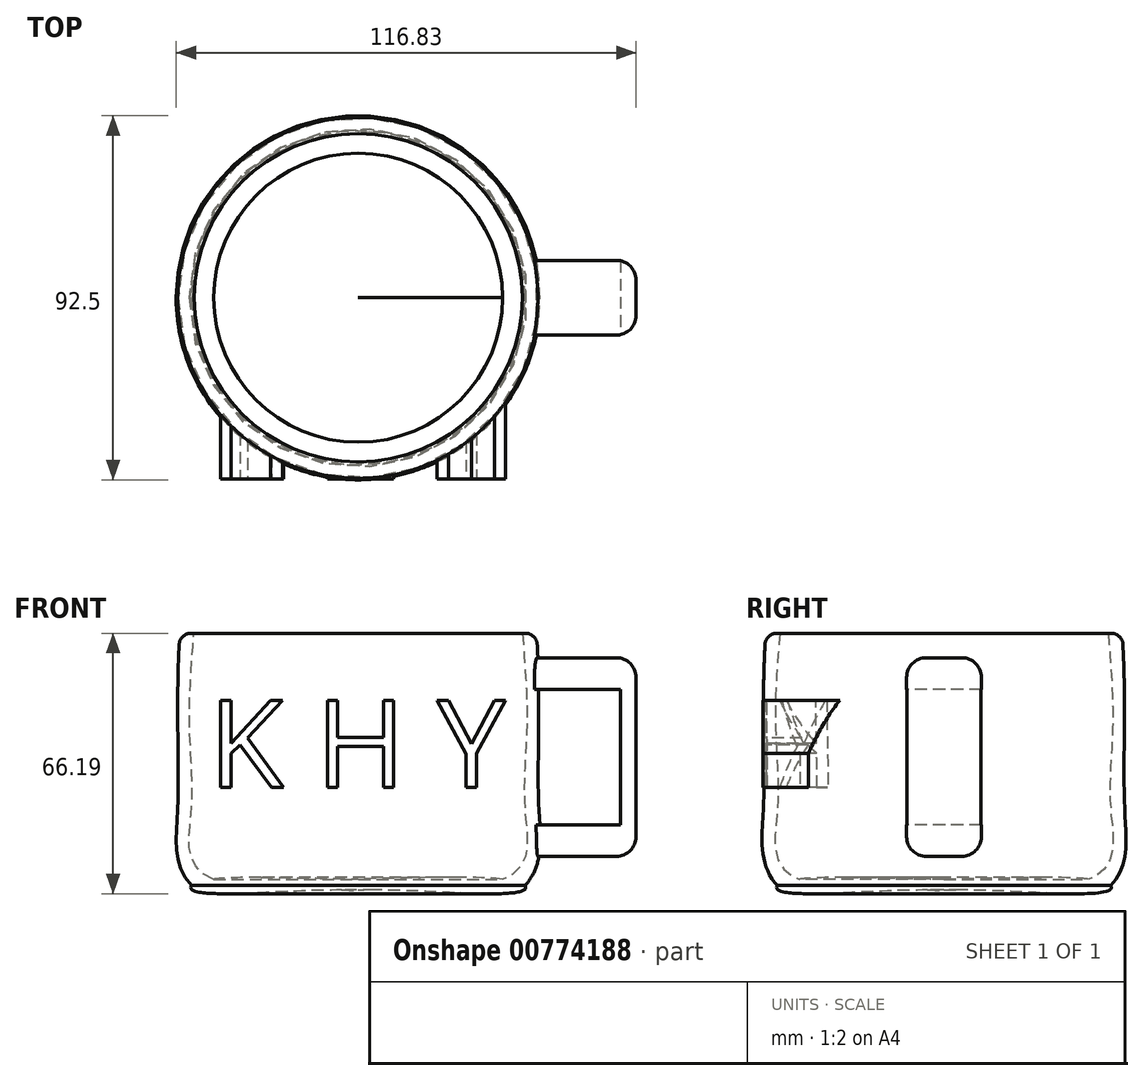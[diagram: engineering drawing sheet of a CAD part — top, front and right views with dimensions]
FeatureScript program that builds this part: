
annotation { "Feature Type Name" : "Feature", "Feature Type Description" : "" }
export const myFeature = defineFeature(function(context is Context, id is Id, definition is map)
    precondition{}
    {
        {
            var Q0;
            Q0=qCreatedBy(makeId("Front.planeOp"),FACE);
            var sketch = newSketch(context, id + "F0", { "sketchPlane" : qUnion([Q0])});
            skFitSpline(sketch, "E0", {"points": [v(46.8, -40.73) * mm, v(50.37, -22.12) * mm, v(50.27, 0) * mm, v(49.24, 29.3) * mm], "startDerivative": vector(47.8, 52.83) * mm, "endDerivative": vector(-8.15, 83.5) * mm});
            skFitSpline(sketch, "E1", {"points": [v(41.12, -39.12) * mm, v(46.8, -21.93) * mm, v(47.27, 0) * mm, v(45.64, 29.3) * mm], "startDerivative": vector(82.12, 31.3) * mm, "endDerivative": vector(-7.4, 88.67) * mm});
            skLineSegment(sketch, "E2", {"start": v(34.9, 23.37) * mm, "end": v(63.82, 23.37) * mm});
            skFitSpline(sketch, "E3", {"points": [v(41.12, -39.12) * mm, v(0, -39.12) * mm], "startDerivative": vector(-18.2, 3.08) * mm, "endDerivative": vector(-26.22, -0.22) * mm});
            skFitSpline(sketch, "E4", {"points": [v(46.8, -40.73) * mm, v(41.12, -42.76) * mm, v(0, -42.12) * mm], "startDerivative": vector(9.3, -14.77) * mm, "endDerivative": vector(-61.18, -3.77) * mm});
            skLineSegment(sketch, "E5", {"start": v(0, 28.24) * mm, "end": v(0, -54.85) * mm});
            skLineSegment(sketch, "E6", {"start": v(4.42, -60.01) * mm, "end": v(4.42, 32.1) * mm});
            skSolve(sketch);
        }
        {
            var Q0;
            {var subQ6=sQuery(id+"F0.wireOp",EDGE,"E0");var subQ9=sQuery(id+"F0.wireOp",EDGE,"E4");var subQ10=makeQuery(id+"F0.imprint","INTERSECT",VERTEX,{"derivedFrom":[subQ6,subQ9]});Q0=makeQuery(id+"F0.imprint","IMPRINT",FACE,{"disambiguationData":[TD([[makeQuery(id+"F0.imprint","IMPRINT",EDGE,{"disambiguationData":[TD([[subQ10,-1.0]])],"derivedFrom":subQ6}),1.0]])]});}
            var Q1;
            Q1=sQuery(id+"F0.wireOp",EDGE,"E6");
            revolve(context, id + "F1", {"surfaceOperationType" : NewSurfaceOperationType.NEW, "entities" : qUnion([Q0]), "axis" : qUnion([Q1]), "revolveType" : RevolveType.FULL});
        }
        {
            var Q0;
            Q0=makeQuery(id+"F1.opRevolve","SWEPT_EDGE",EDGE,{"disambiguationData":[OSD([sQuery(id+"F0.wireOp",EDGE,"E0"),sQuery(id+"F0.wireOp",EDGE,"E2")])]});
            fillet(context, id + "F2", {"entities" : qUnion([Q0]), "radius" : 3 * mm, "tangentPropagation" : true, "allowEdgeOverflow" : false});
        }
        {
            var Q0;
            Q0=qCreatedBy(makeId("Right.planeOp"),FACE);
            cPlane(context, id + "F3", {"entities" : qUnion([Q0]), "cplaneType" : CPlaneType.OFFSET, "offset" : 75 * mm, "width" : 150 * mm, "height" : 150 * mm});
        }
        {
            var Q0;
            Q0=qCreatedBy(id+"F3.planeOp",FACE);
            var sketch = newSketch(context, id + "F4", { "sketchPlane" : qUnion([Q0])});
            skLineSegment(sketch, "E7.bottom", {"start": v(9.5, 9.16) * mm, "end": v(-9.5, 9.16) * mm});
            skLineSegment(sketch, "E7.top", {"start": v(9.5, 17.16) * mm, "end": v(-9.5, 17.16) * mm});
            skLineSegment(sketch, "E7.left", {"start": v(9.5, 9.16) * mm, "end": v(9.5, 17.16) * mm});
            skLineSegment(sketch, "E7.right", {"start": v(-9.5, 9.16) * mm, "end": v(-9.5, 17.16) * mm});
            skPoint(sketch, "E7.middle", {"position": v(0, 13.16) * mm});
            skLineSegment(sketch, "E8.bottom", {"start": v(-9.5, -33.31) * mm, "end": v(9.5, -33.31) * mm});
            skLineSegment(sketch, "E8.top", {"start": v(-9.5, -25.31) * mm, "end": v(9.5, -25.31) * mm});
            skLineSegment(sketch, "E8.left", {"start": v(-9.5, -33.31) * mm, "end": v(-9.5, -25.31) * mm});
            skLineSegment(sketch, "E8.right", {"start": v(9.5, -33.31) * mm, "end": v(9.5, -25.31) * mm});
            skPoint(sketch, "E8.middle", {"position": v(0, -29.31) * mm});
            skSolve(sketch);
        }
        {
            var Q0;
            Q0 = qSketchRegion(id + "F4", true);
            extrude(context, id + "F5", {"entities" : qUnion([Q0]), "operationType" : NewBodyOperationType.ADD, "endBound" : BoundingType.UP_TO_NEXT, "oppositeDirection" : true, "depth" : 25 * mm, "offsetDistance" : 25 * mm});
        }
        {
            var Q0;
            Q0=makeQuery(id+"F5.opExtrude","SWEPT_FACE",FACE,{"disambiguationData":[OSD([sQuery(id+"F4.wireOp",EDGE,"E7.bottom")])]});
            var sketch = newSketch(context, id + "F6", { "sketchPlane" : qUnion([Q0])});
            skLineSegment(sketch, "E9", {"start": v(71, -9.5) * mm, "end": v(71, 9.5) * mm});
            skSolve(sketch);
        }
        {
            var Q0;
            {var subQ0=sQuery(id+"F6.wireOp",EDGE,"E9");Q0=makeQuery(id+"F6.imprint","IMPRINT",FACE,{"disambiguationData":[TD([[makeQuery(id+"F6.imprint","IMPRINT",EDGE,{"derivedFrom":subQ0}),-1.0]])]});}
            extrude(context, id + "F7", {"entities" : qUnion([Q0]), "operationType" : NewBodyOperationType.ADD, "endBound" : BoundingType.UP_TO_NEXT, "depth" : 25 * mm, "offsetDistance" : 25 * mm});
        }
        {
            var Q0;
            Q0=makeQuery(id+"F5.opExtrude","SWEPT_EDGE",EDGE,{"disambiguationData":[OSD([sQuery(id+"F4.wireOp",EDGE,"E7.top"),sQuery(id+"F4.wireOp",EDGE,"E7.left")])]});
            var Q1;
            {var subQ0=sQuery(id+"F4.wireOp",EDGE,"E7.left");Q1=makeQuery(id+"F7.boolean.opBoolean","MERGE",EDGE,{"derivedFrom":[makeQuery(id+"F5.opExtrude","CAP_EDGE",EDGE,{"disambiguationData":[OSD([subQ0])],"isStart":true}),makeQuery(id+"F5.opExtrude","CAP_EDGE",EDGE,{"disambiguationData":[OSD([sQuery(id+"F4.wireOp",EDGE,"E8.right")])],"isStart":true}),makeQuery(id+"F7.opExtrude","SWEPT_EDGE",EDGE,{"disambiguationData":[OSD([sQuery(id+"F4.wireOp",EDGE,"E7.bottom"),subQ0])]})]});}
            var Q2;
            Q2=makeQuery(id+"F5.opExtrude","SWEPT_EDGE",EDGE,{"disambiguationData":[OSD([sQuery(id+"F4.wireOp",EDGE,"E7.top"),sQuery(id+"F4.wireOp",EDGE,"E7.right")])]});
            var Q3;
            {var subQ0=sQuery(id+"F4.wireOp",EDGE,"E8.left");Q3=makeQuery(id+"F7.boolean.opBoolean","MERGE",EDGE,{"derivedFrom":[makeQuery(id+"F5.opExtrude","CAP_EDGE",EDGE,{"disambiguationData":[OSD([sQuery(id+"F4.wireOp",EDGE,"E7.right")])],"isStart":true}),makeQuery(id+"F5.opExtrude","CAP_EDGE",EDGE,{"disambiguationData":[OSD([subQ0])],"isStart":true}),makeQuery(id+"F7.opExtrude","SWEPT_EDGE",EDGE,{"disambiguationData":[OSD([sQuery(id+"F4.wireOp",EDGE,"E8.top"),subQ0])]})]});}
            var Q4;
            Q4=makeQuery(id+"F5.opExtrude","SWEPT_EDGE",EDGE,{"disambiguationData":[OSD([sQuery(id+"F4.wireOp",EDGE,"E8.bottom"),sQuery(id+"F4.wireOp",EDGE,"E8.left")])]});
            var Q5;
            Q5=makeQuery(id+"F5.opExtrude","SWEPT_EDGE",EDGE,{"disambiguationData":[OSD([sQuery(id+"F4.wireOp",EDGE,"E8.bottom"),sQuery(id+"F4.wireOp",EDGE,"E8.right")])]});
            var Q6;
            Q6=makeQuery(id+"F5.opExtrude","CAP_EDGE",EDGE,{"disambiguationData":[OSD([sQuery(id+"F4.wireOp",EDGE,"E8.bottom")])],"isStart":true});
            var Q7;
            Q7=makeQuery(id+"F5.opExtrude","CAP_EDGE",EDGE,{"disambiguationData":[OSD([sQuery(id+"F4.wireOp",EDGE,"E7.top")])],"isStart":true});
            fillet(context, id + "F8", {"entities" : qUnion([Q0, Q1, Q2, Q3, Q4, Q5, Q6, Q7]), "radius" : 5 * mm, "tangentPropagation" : true, "allowEdgeOverflow" : false});
        }
        {
            var Q0;
            Q0=qCreatedBy(makeId("Front.planeOp"),FACE);
            cPlane(context, id + "F9", {"entities" : qUnion([Q0]), "cplaneType" : CPlaneType.OFFSET, "offset" : 46 * mm, "width" : 150 * mm, "height" : 150 * mm});
        }
        {
            var Q0;
            Q0=qCreatedBy(id+"F9.planeOp",FACE);
            var sketch = newSketch(context, id + "F10", { "sketchPlane" : qUnion([Q0])});
            skText(sketch, "E10", { "text": "K H Y\n", "fontName": "OpenSans-Regular.ttf"});
            const initialGuessF10  = {"E10": [-0.03354, -0.01577, 1, 0, 0.02233]};
            skSetInitialGuess(sketch, initialGuessF10);
            skSolve(sketch);
        }
        {
            var Q0;
            Q0 = qSketchRegion(id + "F10", true);
            extrude(context, id + "F11", {"entities" : qUnion([Q0]), "endBound" : BoundingType.UP_TO_NEXT, "oppositeDirection" : true, "depth" : 25 * mm, "offsetDistance" : 25 * mm});
        }
    });
